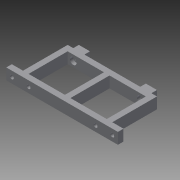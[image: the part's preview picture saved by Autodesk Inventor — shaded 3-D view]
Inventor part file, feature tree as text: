
AUTODESK INVENTOR PART (.ipt)
format: ipt  version: 2013 SP2 (Build 170200200, 200)  size: 131,584 bytes
history: native  units: mm
features: extrude x3, sketch x3
ambient origin geometry x8: Origin, YZ Plane, XZ Plane, XY Plane, X Axis, Y Axis, Z Axis, Center Point
bodies: Solid1 (feature_tree)
feature tree (6):
  extrude  "Extrusion1"  Depth=50.0mm
  extrude  "Extrusion2"  Depth=70.0mm
  extrude  "Extrusion3"  Depth=5.0mm
  sketch  "Sketch1"  dims[d0=80.0mm d1=50.0mm]
  sketch  "Sketch2"  dims[d2=50.0mm d3=70.0mm]
  sketch  "Sketch3"  dims[d4=100.0mm d5=5.0mm d6=5.0mm d7=5.0mm d8=10.0mm d9=0.0mm d10=5.0mm d11=5.0mm d12=5.0mm d13=3.4mm d15=10.0mm d16=0.0mm d17=6.0mm d18=6.0mm d19=3.0mm d20=0.0mm]
